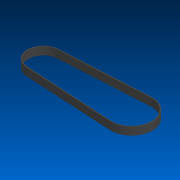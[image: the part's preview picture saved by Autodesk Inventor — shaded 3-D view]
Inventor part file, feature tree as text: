
AUTODESK INVENTOR PART (.ipt)
format: ipt  version: 2022.2 (Build 262287000, 287)  size: 98,304 bytes
history: native  units: in
note: dims shown in document units (in); Inventor stores cm internally (conversion verified against a paired STEP export)
features: extrude x1, sketch x1
ambient origin geometry x8: Origin, YZ Plane, XZ Plane, XY Plane, X Axis, Y Axis, Z Axis, Center Point
bodies: Solid1 (feature_tree)
feature tree (2):
  extrude  "Extrusion1"  Depth=0.0394in
  sketch  "Sketch1"  dims[d0=3.9805in d1=1.353in d2=1.805in d4=0.3543in d5=0.0in d6=0.0394in]
